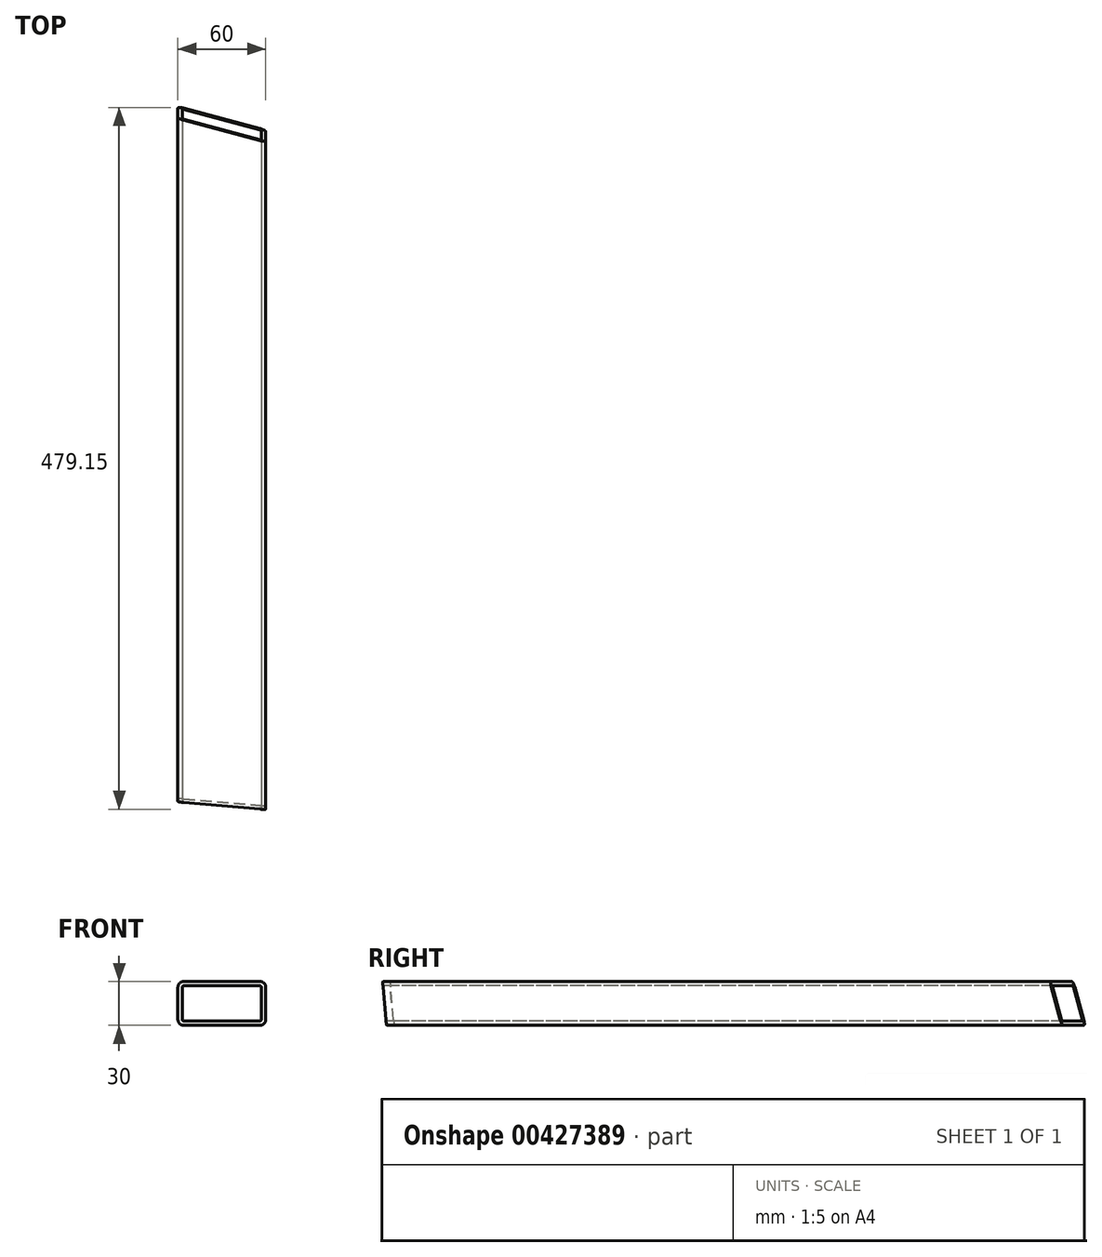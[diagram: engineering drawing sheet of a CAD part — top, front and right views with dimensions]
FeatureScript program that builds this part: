
annotation { "Feature Type Name" : "Feature", "Feature Type Description" : "" }
export const myFeature = defineFeature(function(context is Context, id is Id, definition is map)
    precondition{}
    {
        {
            var Q0;
            Q0=qCreatedBy(makeId("Front.planeOp"),FACE);
            var sketch = newSketch(context, id + "F0", { "sketchPlane" : qUnion([Q0])});
            skLineSegment(sketch, "E0.bottom", {"start": v(26, 15) * mm, "end": v(-26, 15) * mm});
            skLineSegment(sketch, "E0.top", {"start": v(26, -15) * mm, "end": v(-26, -15) * mm});
            skLineSegment(sketch, "E0.left", {"start": v(30, 11) * mm, "end": v(30, -11) * mm});
            skLineSegment(sketch, "E0.right", {"start": v(-30, 11) * mm, "end": v(-30, -11) * mm});
            skPoint(sketch, "E0.middle", {"position": v(0, 0) * mm});
            skPoint(sketch, "E1.visualSharp", {"position": v(-30, 15) * mm});
            skArc(sketch, "E1.filletArc", {"start": v(-26, 15) * mm, "mid": v(-28.83, 13.83) * mm, "end": v(-30, 11) * mm});
            skPoint(sketch, "E2.visualSharp", {"position": v(30, 15) * mm});
            skArc(sketch, "E2.filletArc", {"start": v(30, 11) * mm, "mid": v(28.83, 13.83) * mm, "end": v(26, 15) * mm});
            skPoint(sketch, "E3.visualSharp", {"position": v(30, -15) * mm});
            skArc(sketch, "E3.filletArc", {"start": v(26, -15) * mm, "mid": v(28.83, -13.83) * mm, "end": v(30, -11) * mm});
            skPoint(sketch, "E4.visualSharp", {"position": v(-30, -15) * mm});
            skArc(sketch, "E4.filletArc", {"start": v(-30, -11) * mm, "mid": v(-28.83, -13.83) * mm, "end": v(-26, -15) * mm});
            skArc(sketch, "E5.0", {"start": v(-26, 12) * mm, "mid": v(-26.7, 11.7) * mm, "end": v(-27, 11) * mm});
            skLineSegment(sketch, "E5.1", {"start": v(26, 12) * mm, "end": v(-26, 12) * mm});
            skLineSegment(sketch, "E5.2", {"start": v(-27, 11) * mm, "end": v(-27, -11) * mm});
            skArc(sketch, "E5.3", {"start": v(27, 11) * mm, "mid": v(26.7, 11.7) * mm, "end": v(26, 12) * mm});
            skArc(sketch, "E5.4", {"start": v(-27, -11) * mm, "mid": v(-26.7, -11.7) * mm, "end": v(-26, -12) * mm});
            skLineSegment(sketch, "E5.5", {"start": v(26, -12) * mm, "end": v(-26, -12) * mm});
            skArc(sketch, "E5.6", {"start": v(26, -12) * mm, "mid": v(26.7, -11.7) * mm, "end": v(27, -11) * mm});
            skLineSegment(sketch, "E5.7", {"start": v(27, 11) * mm, "end": v(27, -11) * mm});
            skSolve(sketch);
        }
        {
            var Q0;
            Q0=makeQuery(id+"F0.imprint","IMPRINT",FACE,{"disambiguationData":[TD([[makeQuery(id+"F0.imprint","IMPRINT",EDGE,{"derivedFrom":sQuery(id+"F0.wireOp",EDGE,"E0.bottom")}),1.0]])]});
            extrude(context, id + "F1", {"entities" : qUnion([Q0]), "endBound" : BoundingType.SYMMETRIC, "oppositeDirection" : true, "depth" : (490 - 10) * mm});
        }
        {
            var Q0;
            Q0=makeQuery(id+"F1.opExtrude","SWEPT_FACE",FACE,{"disambiguationData":[OSD([sQuery(id+"F0.wireOp",EDGE,"E0.bottom")])]});
            var sketch = newSketch(context, id + "F2", { "sketchPlane" : qUnion([Q0])});
            skLineSegment(sketch, "E6.0", {"start": v(26, -240) * mm, "end": v(-26, -240) * mm});
            skLineSegment(sketch, "E7.0", {"start": v(30, -240) * mm, "end": v(26, -240) * mm});
            skLineSegment(sketch, "E8.0", {"start": v(-26, -240) * mm, "end": v(-30, -240) * mm});
            skLineSegment(sketch, "E9", {"start": v(-30, -240) * mm, "end": v(-30, -234.75) * mm});
            skLineSegment(sketch, "E10", {"start": v(-30, -234.75) * mm, "end": v(30, -240) * mm});
            skSolve(sketch);
        }
        {
            var Q0;
            {var subQ0=sQuery(id+"F2.wireOp",EDGE,"E6.0");Q0=makeQuery(id+"F2.imprint","IMPRINT",FACE,{"disambiguationData":[TD([[makeQuery(id+"F2.imprint","IMPRINT",EDGE,{"derivedFrom":subQ0}),-1.0]])]});}
            var Q1;
            {var subQ0=sQuery(id+"F2.wireOp",EDGE,"E8.0");Q1=makeQuery(id+"F2.imprint","IMPRINT",FACE,{"disambiguationData":[TD([[makeQuery(id+"F2.imprint","IMPRINT",EDGE,{"derivedFrom":subQ0}),-1.0]])]});}
            var Q2;
            {var subQ0=sQuery(id+"F2.wireOp",EDGE,"E7.0");Q2=makeQuery(id+"F2.imprint","IMPRINT",FACE,{"disambiguationData":[TD([[makeQuery(id+"F2.imprint","IMPRINT",EDGE,{"derivedFrom":subQ0}),-1.0]])]});}
            extrude(context, id + "F3", {"entities" : qUnion([Q0, Q1, Q2]), "operationType" : NewBodyOperationType.REMOVE, "oppositeDirection" : true, "depth" : 30 * mm});
        }
        {
            var Q0;
            Q0=makeQuery(id+"F3.boolean.opBoolean","MERGE",EDGE,{"derivedFrom":[makeQuery(id+"F1.opExtrude","CAP_EDGE",EDGE,{"disambiguationData":[OSD([sQuery(id+"F0.wireOp",EDGE,"E0.left")])],"isStart":true}),makeQuery(id+"F3.opExtrude","SWEPT_EDGE",EDGE,{"disambiguationData":[OSD([sQuery(id+"F2.wireOp",EDGE,"E7.0"),sQuery(id+"F2.wireOp",EDGE,"E10")])]})]});
            cPlane(context, id + "F4", {"entities" : qUnion([Q0]), "cplaneType" : CPlaneType.LINE_ANGLE, "offset" : 25 * mm, "angle" : 5 * degree, "width" : 150 * mm, "height" : 150 * mm});
        }
        {
            var Q0;
            Q0=qCreatedBy(id+"F4.planeOp",FACE);
            var sketch = newSketch(context, id + "F5", { "sketchPlane" : qUnion([Q0])});
            skLineSegment(sketch, "E11.0", {"start": v(236.47, -11) * mm, "end": v(236.47, -15) * mm});
            skLineSegment(sketch, "E12.0", {"start": v(236.47, 11) * mm, "end": v(236.47, -11) * mm});
            skLineSegment(sketch, "E13.0", {"start": v(236.47, 15) * mm, "end": v(236.47, 11) * mm});
            skPoint(sketch, "E14.orphan", {"position": v(-241.35, -15) * mm});
            skPoint(sketch, "E15.orphan", {"position": v(-241.35, 15) * mm});
            skLineSegment(sketch, "E16.0", {"start": v(233.85, -15) * mm, "end": v(236.47, -15) * mm});
            skLineSegment(sketch, "E17", {"start": v(236.47, 15) * mm, "end": v(233.85, -15) * mm});
            skSolve(sketch);
        }
        {
            var Q0;
            Q0=makeQuery(id+"F5.imprint","IMPRINT",FACE,{"disambiguationData":[TD([[makeQuery(id+"F5.imprint","IMPRINT",EDGE,{"derivedFrom":sQuery(id+"F5.wireOp",EDGE,"E11.0")}),-1.0]])]});
            extrude(context, id + "F6", {"entities" : qUnion([Q0]), "operationType" : NewBodyOperationType.REMOVE, "depth" : 70 * mm});
        }
        {
            var Q0;
            Q0=makeQuery(id+"F1.opExtrude","SWEPT_FACE",FACE,{"disambiguationData":[OSD([sQuery(id+"F0.wireOp",EDGE,"E0.top")])]});
            var sketch = newSketch(context, id + "F7", { "sketchPlane" : qUnion([Q0])});
            skCircle(sketch, "E18", {"center": v(-4.87, 149.92) * mm, "radius": 7.35 * mm});
            skSolve(sketch);
        }
        {
            var Q0;
            Q0=makeQuery(id+"F1.opExtrude","SWEPT_FACE",FACE,{"disambiguationData":[OSD([sQuery(id+"F0.wireOp",EDGE,"E0.top")])]});
            var sketch = newSketch(context, id + "F8", { "sketchPlane" : qUnion([Q0])});
            skLineSegment(sketch, "E19.0", {"start": v(26, -240) * mm, "end": v(-26, -240) * mm});
            skLineSegment(sketch, "E20.0", {"start": v(-30, -240) * mm, "end": v(-26, -240) * mm});
            skLineSegment(sketch, "E21.0", {"start": v(26, -240) * mm, "end": v(30, -240) * mm});
            skPoint(sketch, "E22.orphan", {"position": v(30, 237.72) * mm});
            skPoint(sketch, "E23.orphan", {"position": v(-30, 232.47) * mm});
            skLineSegment(sketch, "E24", {"start": v(30, -240) * mm, "end": v(30, -223.92) * mm});
            skLineSegment(sketch, "E25", {"start": v(30, -223.92) * mm, "end": v(-30, -240) * mm});
            skSolve(sketch);
        }
        {
            var Q0;
            {var subQ0=sQuery(id+"F8.wireOp",EDGE,"E19.0");Q0=makeQuery(id+"F8.imprint","IMPRINT",FACE,{"disambiguationData":[TD([[makeQuery(id+"F8.imprint","IMPRINT",EDGE,{"derivedFrom":subQ0}),-1.0]])]});}
            var Q1;
            {var subQ0=sQuery(id+"F8.wireOp",EDGE,"E21.0");Q1=makeQuery(id+"F8.imprint","IMPRINT",FACE,{"disambiguationData":[TD([[makeQuery(id+"F8.imprint","IMPRINT",EDGE,{"derivedFrom":subQ0}),1.0]])]});}
            var Q2;
            {var subQ0=sQuery(id+"F8.wireOp",EDGE,"E20.0");Q2=makeQuery(id+"F8.imprint","IMPRINT",FACE,{"disambiguationData":[TD([[makeQuery(id+"F8.imprint","IMPRINT",EDGE,{"derivedFrom":subQ0}),1.0]])]});}
            extrude(context, id + "F9", {"entities" : qUnion([Q0, Q1, Q2]), "operationType" : NewBodyOperationType.REMOVE, "endBound" : BoundingType.THROUGH_ALL, "oppositeDirection" : true, "depth" : 25 * mm});
        }
        {
            var Q0;
            Q0=makeQuery(id+"F9.boolean.opBoolean","MERGE",EDGE,{"derivedFrom":[makeQuery(id+"F1.opExtrude","CAP_EDGE",EDGE,{"disambiguationData":[OSD([sQuery(id+"F0.wireOp",EDGE,"E0.right")])],"isStart":false}),makeQuery(id+"F9.opExtrude","SWEPT_EDGE",EDGE,{"disambiguationData":[OSD([sQuery(id+"F8.wireOp",EDGE,"E20.0"),sQuery(id+"F8.wireOp",EDGE,"E25")])]})]});
            cPlane(context, id + "F10", {"entities" : qUnion([Q0]), "cplaneType" : CPlaneType.LINE_ANGLE, "offset" : 25 * mm, "angle" : 15 * degree, "width" : 150 * mm, "height" : 150 * mm});
        }
        {
            var Q0;
            Q0=qCreatedBy(id+"F10.planeOp",FACE);
            var sketch = newSketch(context, id + "F11", { "sketchPlane" : qUnion([Q0])});
            skLineSegment(sketch, "E26.0", {"start": v(-224.06, 15) * mm, "end": v(-216.02, 15) * mm});
            skLineSegment(sketch, "E27", {"start": v(-224.06, -15) * mm, "end": v(-216.02, 15) * mm});
            skLineSegment(sketch, "E28.0", {"start": v(-224.06, 11) * mm, "end": v(-224.06, -11) * mm});
            skLineSegment(sketch, "E29.0", {"start": v(-224.06, -15) * mm, "end": v(-224.06, -11) * mm});
            skLineSegment(sketch, "E30.0", {"start": v(-224.06, 11) * mm, "end": v(-224.06, 15) * mm});
            skSolve(sketch);
        }
        {
            var Q0;
            Q0=qSketchRegion(id+"F11",true);
            extrude(context, id + "F12", {"entities" : qUnion([Q0]), "operationType" : NewBodyOperationType.REMOVE, "endBound" : BoundingType.SYMMETRIC, "oppositeDirection" : true, "depth" : 200 * mm});
        }
    });
